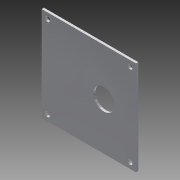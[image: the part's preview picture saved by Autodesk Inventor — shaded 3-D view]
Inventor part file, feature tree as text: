
AUTODESK INVENTOR PART (.ipt)
format: ipt  version: 2015 (Build 190159000, 159)  size: 114,176 bytes
history: native  units: in
note: dims shown in document units (in); Inventor stores cm internally (conversion verified against a paired STEP export)
features: other x3, hole x2, sketch x1
ambient origin geometry x8: Origin, YZ Plane, XZ Plane, XY Plane, X Axis, Y Axis, Z Axis, Center Point
bodies: Solid1 (feature_tree)
feature tree (6):
  hole  "gbmh"  [1 undecoded]
  hole  "ss_bearing_hole"  [1 undecoded]
  sketch  "Sketch1"  dims[d0=5.0in d1=0.12in d2=4.376in d3=4.376in d4=4.376in d5=4.376in d6=0.25in d7=0.75in d8=0.375in d9=0.25in d10=0.5635in d11=0.12in d12=0.8108in d13=1.5in d14=1.5in d15=1.125in d16=0.75in d17=0.375in d18=0.25in d19=0.5635in d20=0.12in d21=0.8108in]
  other  "Plate1"
  other  "gbmh_sketch"
  other  "bearing_hole_sketch"
note: 2 required parameter values undecoded (feature->parameter linkage not recoverable at this tier; creation-order binding heuristic only, values carry confidence <= 0.55)
